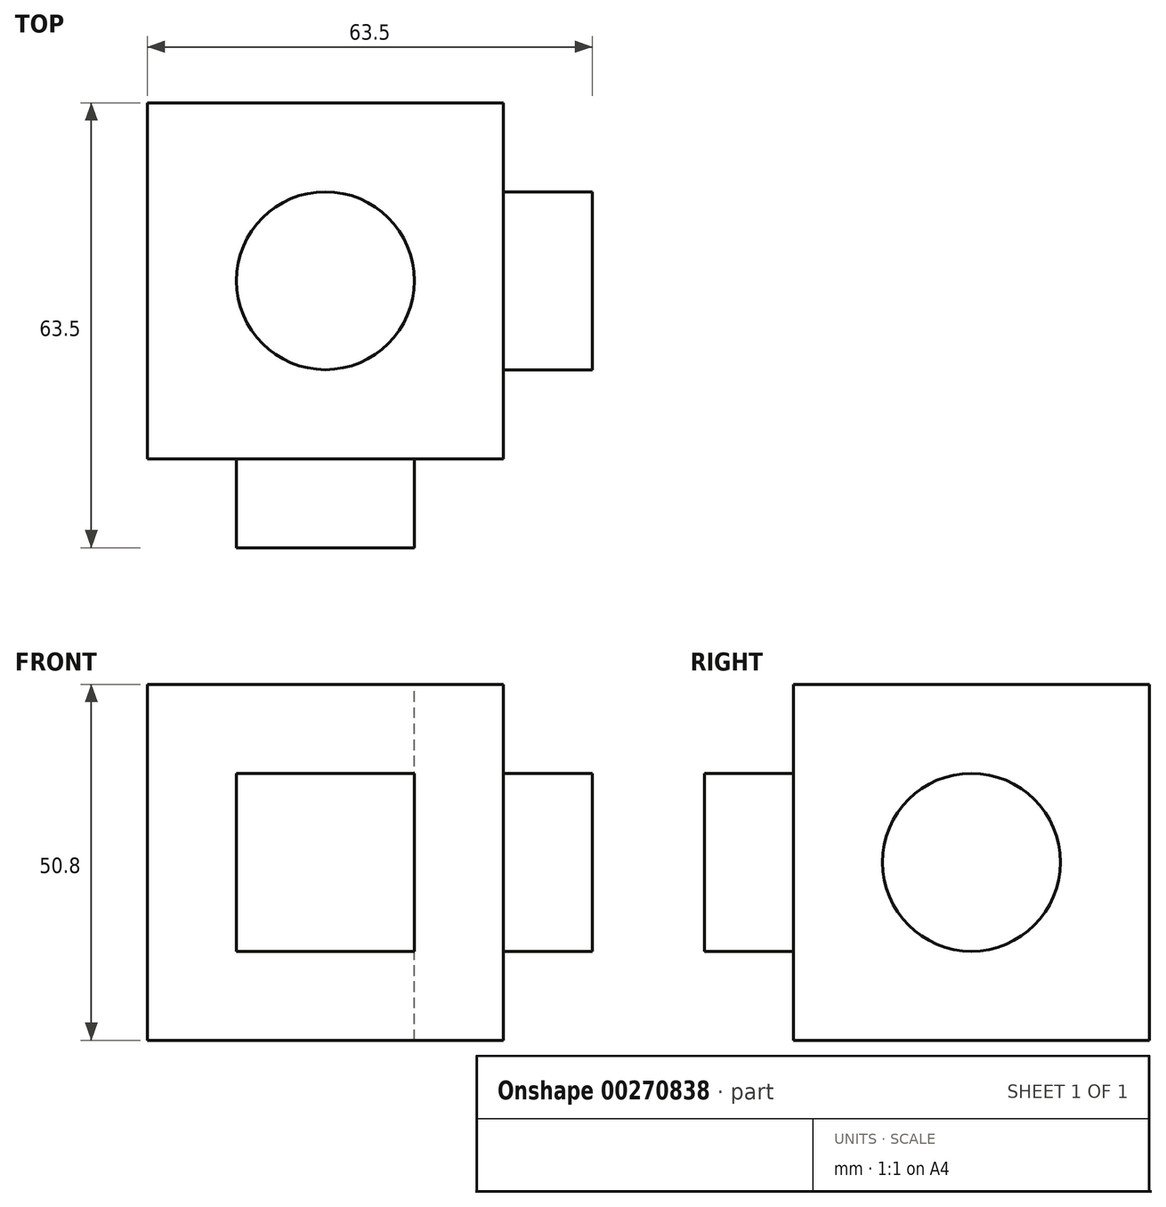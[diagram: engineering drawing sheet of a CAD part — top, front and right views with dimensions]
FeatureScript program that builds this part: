
annotation { "Feature Type Name" : "Feature", "Feature Type Description" : "" }
export const myFeature = defineFeature(function(context is Context, id is Id, definition is map)
    precondition{}
    {
        {
            var Q0;
            Q0=qCreatedBy(makeId("Front.planeOp"),FACE);
            var sketch = newSketch(context, id + "F0", { "sketchPlane" : qUnion([Q0])});
            skLineSegment(sketch, "E0.bottom", {"start": v(0, 0) * mm, "end": v(-50.8, 0) * mm});
            skLineSegment(sketch, "E0.top", {"start": v(0, 50.8) * mm, "end": v(-50.8, 50.8) * mm});
            skLineSegment(sketch, "E0.left", {"start": v(0, 0) * mm, "end": v(0, 50.8) * mm});
            skLineSegment(sketch, "E0.right", {"start": v(-50.8, 0) * mm, "end": v(-50.8, 50.8) * mm});
            skSolve(sketch);
        }
        {
            var Q0;
            Q0 = qSketchRegion(id + "F0", true);
            extrude(context, id + "F1", {"entities" : qUnion([Q0]), "depth" : 50.8 * mm});
        }
        {
            var Q0;
            Q0=makeQuery(id+"F1.opExtrude","SWEPT_FACE",FACE,{"disambiguationData":[OSD([sQuery(id+"F0.wireOp",EDGE,"E0.top")])]});
            var sketch = newSketch(context, id + "F2", { "sketchPlane" : qUnion([Q0])});
            skCircle(sketch, "E1", {"center": v(-25.4, -25.4) * mm, "radius": 12.7 * mm});
            skSolve(sketch);
        }
        {
            var Q0;
            Q0 = qSketchRegion(id + "F2", true);
            extrude(context, id + "F3", {"entities" : qUnion([Q0]), "operationType" : NewBodyOperationType.REMOVE, "oppositeDirection" : true, "depth" : 50.8 * mm});
        }
        {
            var Q0;
            Q0=makeQuery(id+"F1.opExtrude","CAP_FACE",FACE,{"disambiguationData":[OSD([sQuery(id+"F0.wireOp",EDGE,"E0.bottom"),sQuery(id+"F0.wireOp",EDGE,"E0.top"),sQuery(id+"F0.wireOp",EDGE,"E0.left"),sQuery(id+"F0.wireOp",EDGE,"E0.right")])],"isStart":false});
            var sketch = newSketch(context, id + "F4", { "sketchPlane" : qUnion([Q0])});
            skLineSegment(sketch, "E2.bottom", {"start": v(-38.1, 38.1) * mm, "end": v(-12.7, 38.1) * mm});
            skLineSegment(sketch, "E2.top", {"start": v(-38.1, 12.7) * mm, "end": v(-12.7, 12.7) * mm});
            skLineSegment(sketch, "E2.left", {"start": v(-38.1, 38.1) * mm, "end": v(-38.1, 12.7) * mm});
            skLineSegment(sketch, "E2.right", {"start": v(-12.7, 38.1) * mm, "end": v(-12.7, 12.7) * mm});
            skSolve(sketch);
        }
        {
            var Q0;
            Q0=makeQuery(id+"F1.opExtrude","SWEPT_FACE",FACE,{"disambiguationData":[OSD([sQuery(id+"F0.wireOp",EDGE,"E0.left")])]});
            var sketch = newSketch(context, id + "F5", { "sketchPlane" : qUnion([Q0])});
            skCircle(sketch, "E3", {"center": v(-25.4, 25.4) * mm, "radius": 12.7 * mm});
            skSolve(sketch);
        }
        {
            var Q0;
            Q0 = qSketchRegion(id + "F5", true);
            extrude(context, id + "F6", {"entities" : qUnion([Q0]), "operationType" : NewBodyOperationType.ADD, "depth" : 12.7 * mm});
        }
        {
            var Q0;
            Q0 = qSketchRegion(id + "F4", true);
            extrude(context, id + "F7", {"entities" : qUnion([Q0]), "operationType" : NewBodyOperationType.ADD, "depth" : 12.7 * mm});
        }
    });
